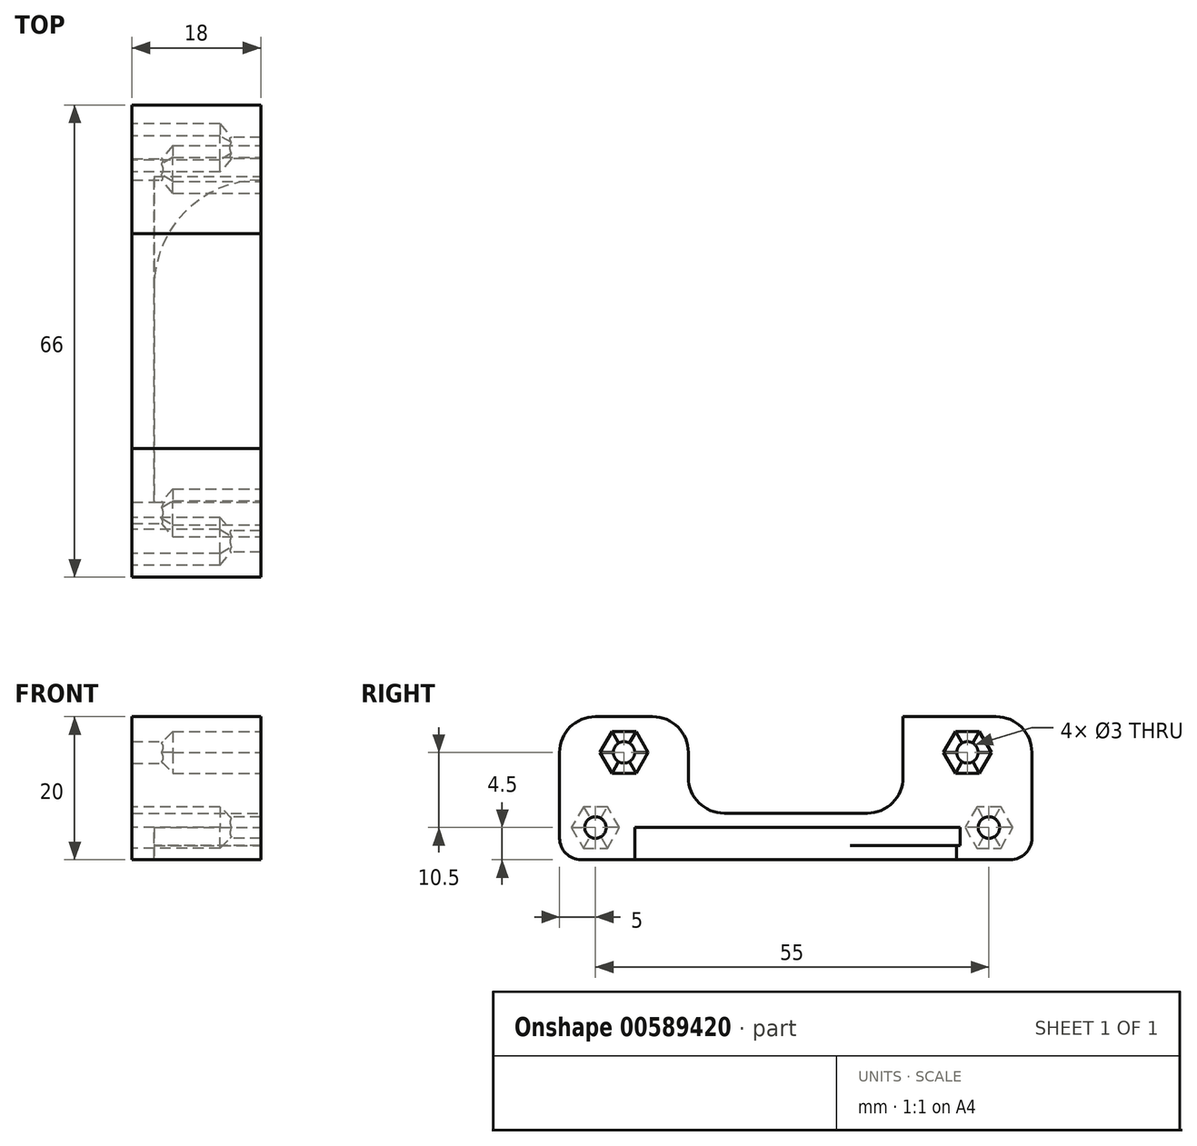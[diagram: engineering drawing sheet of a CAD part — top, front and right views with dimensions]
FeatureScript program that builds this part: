
annotation { "Feature Type Name" : "Feature", "Feature Type Description" : "" }
export const myFeature = defineFeature(function(context is Context, id is Id, definition is map)
    precondition{}
    {
        {
            var Q0;
            Q0=qCreatedBy(makeId("Right.planeOp"),FACE);
            var sketch = newSketch(context, id + "F0", { "sketchPlane" : qUnion([Q0])});
            skLineSegment(sketch, "E0", {"start": v(0, 0) * mm, "end": v(0, 20) * mm});
            skLineSegment(sketch, "E1", {"start": v(0, 20) * mm, "end": v(10, 20) * mm});
            skLineSegment(sketch, "E2", {"start": v(10, 20) * mm, "end": v(10, 18) * mm});
            skLineSegment(sketch, "E3", {"start": v(10, 18) * mm, "end": v(5, 18) * mm});
            skLineSegment(sketch, "E4", {"start": v(5, 18) * mm, "end": v(5, 9) * mm});
            skLineSegment(sketch, "E5", {"start": v(5, 9) * mm, "end": v(66, 9) * mm});
            skLineSegment(sketch, "E6", {"start": v(66, 9) * mm, "end": v(66, 0) * mm});
            skLineSegment(sketch, "E7", {"start": v(66, 0) * mm, "end": v(0, 0) * mm});
            skLineSegment(sketch, "E8", {"start": v(66, 9) * mm, "end": v(66, 20) * mm});
            skLineSegment(sketch, "E9", {"start": v(66, 20) * mm, "end": v(10, 20) * mm});
            skSolve(sketch);
        }
        {
            var Q0;
            Q0=makeQuery(id+"F0.imprint","IMPRINT",FACE,{"disambiguationData":[TD([[makeQuery(id+"F0.imprint","IMPRINT",EDGE,{"derivedFrom":sQuery(id+"F0.wireOp",EDGE,"E0")}),-1.0]])]});
            var Q1;
            Q1=makeQuery(id+"F0.imprint","IMPRINT",FACE,{"disambiguationData":[TD([[makeQuery(id+"F0.imprint","IMPRINT",EDGE,{"derivedFrom":sQuery(id+"F0.wireOp",EDGE,"E2")}),1.0]])]});
            extrude(context, id + "F1", {"entities" : qUnion([Q0, Q1]), "oppositeDirection" : true, "depth" : 16 * mm, "offsetDistance" : 25 * mm});
        }
        {
            var Q0;
            Q0=makeQuery(id+"F1.opExtrude","CAP_FACE",FACE,{"disambiguationData":[OSD([sQuery(id+"F0.wireOp",EDGE,"E0"),sQuery(id+"F0.wireOp",EDGE,"E1"),sQuery(id+"F0.wireOp",EDGE,"E2"),sQuery(id+"F0.wireOp",EDGE,"E3"),sQuery(id+"F0.wireOp",EDGE,"E4"),sQuery(id+"F0.wireOp",EDGE,"E5"),sQuery(id+"F0.wireOp",EDGE,"E6"),sQuery(id+"F0.wireOp",EDGE,"E7")])],"isStart":true});
            var sketch = newSketch(context, id + "F2", { "sketchPlane" : qUnion([Q0])});
            skLineSegment(sketch, "E10.0", {"start": v(66, 0) * mm, "end": v(0, 0) * mm});
            skLineSegment(sketch, "E11", {"start": v(10.5, 0) * mm, "end": v(10.5, 4.5) * mm});
            skLineSegment(sketch, "E12", {"start": v(10.5, 4.5) * mm, "end": v(56, 4.5) * mm});
            skLineSegment(sketch, "E13", {"start": v(56, 4.5) * mm, "end": v(56, 2) * mm});
            skLineSegment(sketch, "E14", {"start": v(56, 2) * mm, "end": v(55.5, 2) * mm});
            skLineSegment(sketch, "E15", {"start": v(55.5, 2) * mm, "end": v(55.5, 0) * mm});
            skSolve(sketch);
        }
        {
            var Q0;
            {var subQ0=sQuery(id+"F2.wireOp",EDGE,"E11");Q0=makeQuery(id+"F2.imprint","IMPRINT",FACE,{"disambiguationData":[TD([[makeQuery(id+"F2.imprint","IMPRINT",EDGE,{"derivedFrom":subQ0}),-1.0]])]});}
            extrude(context, id + "F3", {"entities" : qUnion([Q0]), "operationType" : NewBodyOperationType.REMOVE, "oppositeDirection" : true, "depth" : 14.9 * mm});
        }
        {
            var Q0;
            Q0=makeQuery(id+"F1.opExtrude","SWEPT_FACE",FACE,{"disambiguationData":[OSD([sQuery(id+"F0.wireOp",EDGE,"E7")])]});
            var sketch = newSketch(context, id + "F4", { "sketchPlane" : qUnion([Q0])});
            skLineSegment(sketch, "E16.0", {"start": v(-14.9, -55.5) * mm, "end": v(0, -55.5) * mm});
            skLineSegment(sketch, "E17.0", {"start": v(-14.9, -55.5) * mm, "end": v(-14.9, -10.5) * mm});
            skArc(sketch, "E18", {"start": v(-14.9, -40.6) * mm, "mid": v(-10.54, -51.14) * mm, "end": v(0, -55.5) * mm});
            skSolve(sketch);
        }
        {
            var Q0;
            {var subQ0=sQuery(id+"F4.wireOp",EDGE,"E16.0");Q0=makeQuery(id+"F4.imprint","IMPRINT",FACE,{"disambiguationData":[TD([[makeQuery(id+"F4.imprint","IMPRINT",EDGE,{"derivedFrom":subQ0}),1.0]])]});}
            var Q1;
            Q1=makeQuery(id+"F3.boolean.opBoolean","COPY",FACE,{"derivedFrom":makeQuery(id+"F3.opExtrude","SWEPT_FACE",FACE,{"disambiguationData":[OSD([sQuery(id+"F2.wireOp",EDGE,"E14")])]})});
            extrude(context, id + "F5", {"entities" : qUnion([Q0]), "operationType" : NewBodyOperationType.ADD, "endBound" : BoundingType.UP_TO_SURFACE, "oppositeDirection" : true, "endBoundEntityFace" : qUnion([Q1]), "depth" : 2 * mm});
        }
        {
            var Q0;
            Q0=makeQuery(id+"F1.opExtrude","CAP_FACE",FACE,{"disambiguationData":[OSD([sQuery(id+"F0.wireOp",EDGE,"E0"),sQuery(id+"F0.wireOp",EDGE,"E1"),sQuery(id+"F0.wireOp",EDGE,"E2"),sQuery(id+"F0.wireOp",EDGE,"E3"),sQuery(id+"F0.wireOp",EDGE,"E4"),sQuery(id+"F0.wireOp",EDGE,"E5"),sQuery(id+"F0.wireOp",EDGE,"E6"),sQuery(id+"F0.wireOp",EDGE,"E7")])],"isStart":false});
            var sketch = newSketch(context, id + "F6", { "sketchPlane" : qUnion([Q0])});
            skLineSegment(sketch, "E19.0", {"start": v(-66, 0) * mm, "end": v(0, 0) * mm});
            skLineSegment(sketch, "E20.0", {"start": v(0, 0) * mm, "end": v(0, 20) * mm});
            skLineSegment(sketch, "E21", {"start": v(-66, 0) * mm, "end": v(-66, 20) * mm});
            skLineSegment(sketch, "E22", {"start": v(-66, 20) * mm, "end": v(0, 20) * mm});
            skSolve(sketch);
        }
        {
            var Q0;
            {var subQ2=sQuery(id+"F6.wireOp",EDGE,"E19.0");Q0=makeQuery(id+"F6.imprint","IMPRINT",FACE,{"disambiguationData":[TD([[makeQuery(id+"F6.imprint","IMPRINT",EDGE,{"derivedFrom":subQ2}),1.0]])]});}
            var Q1;
            {var subQ0=makeQuery(id+"F1.opExtrude","CAP_EDGE",EDGE,{"disambiguationData":[OSD([sQuery(id+"F0.wireOp",EDGE,"E2")])],"isStart":false});Q1=makeQuery(id+"F6.imprint","IMPRINT",FACE,{"disambiguationData":[TD([[makeQuery(id+"F6.imprint","IMPRINT",EDGE,{"derivedFrom":subQ0}),-1.0]])]});}
            extrude(context, id + "F7", {"entities" : qUnion([Q0, Q1]), "operationType" : NewBodyOperationType.ADD, "depth" : 2 * mm, "offsetDistance" : 25 * mm});
        }
        {
            var Q0;
            Q0=makeQuery(id+"F7.boolean.opBoolean","MERGE",EDGE,{"derivedFrom":[makeQuery(id+"F1.opExtrude","SWEPT_EDGE",EDGE,{"disambiguationData":[OSD([sQuery(id+"F0.wireOp",EDGE,"E6"),sQuery(id+"F0.wireOp",EDGE,"E7")])]}),makeQuery(id+"F7.opExtrude","SWEPT_EDGE",EDGE,{"disambiguationData":[OSD([sQuery(id+"F6.wireOp",EDGE,"E19.0"),sQuery(id+"F6.wireOp",EDGE,"E21")])]})]});
            var Q1;
            Q1=makeQuery(id+"F3.boolean.opBoolean","COPY",EDGE,{"derivedFrom":makeQuery(id+"F3.opExtrude","SWEPT_EDGE",EDGE,{"disambiguationData":[OSD([sQuery(id+"F2.wireOp",EDGE,"E10.0"),sQuery(id+"F2.wireOp",EDGE,"E11")])]})});
            var Q2;
            Q2=makeQuery(id+"F7.boolean.opBoolean","MERGE",EDGE,{"derivedFrom":[makeQuery(id+"F1.opExtrude","SWEPT_EDGE",EDGE,{"disambiguationData":[OSD([sQuery(id+"F0.wireOp",EDGE,"E0"),sQuery(id+"F0.wireOp",EDGE,"E7")])]}),makeQuery(id+"F7.opExtrude","SWEPT_EDGE",EDGE,{"disambiguationData":[OSD([sQuery(id+"F6.wireOp",EDGE,"E19.0"),sQuery(id+"F6.wireOp",EDGE,"E20.0")])]})]});
            fillet(context, id + "F8", {"entities" : qUnion([Q0, Q1, Q2]), "radius" : 3 * mm, "tangentPropagation" : true, "allowEdgeOverflow" : false});
        }
        {
            var Q0;
            Q0=makeQuery(id+"F7.opExtrude","CAP_FACE",FACE,{"disambiguationData":[OSD([sQuery(id+"F6.wireOp",EDGE,"E19.0"),sQuery(id+"F6.wireOp",EDGE,"E20.0"),sQuery(id+"F6.wireOp",EDGE,"E21"),sQuery(id+"F6.wireOp",EDGE,"E22")])],"isStart":false});
            var sketch = newSketch(context, id + "F9", { "sketchPlane" : qUnion([Q0])});
            skCircle(sketch, "E23.cCircle", {"center": v(-60, 4.5) * mm, "radius": 2.9 * mm, "construction": true});
            skLineSegment(sketch, "E23.0", {"start": v(-63.35, 4.5) * mm, "end": v(-61.67, 7.4) * mm});
            skLineSegment(sketch, "E23.1", {"start": v(-61.67, 7.4) * mm, "end": v(-58.33, 7.4) * mm});
            skLineSegment(sketch, "E23.2", {"start": v(-58.33, 7.4) * mm, "end": v(-56.65, 4.5) * mm});
            skLineSegment(sketch, "E23.3", {"start": v(-56.65, 4.5) * mm, "end": v(-58.33, 1.6) * mm});
            skLineSegment(sketch, "E23.4", {"start": v(-58.33, 1.6) * mm, "end": v(-61.67, 1.6) * mm});
            skLineSegment(sketch, "E23.5", {"start": v(-61.67, 1.6) * mm, "end": v(-63.35, 4.5) * mm});
            skPoint(sketch, "E23.0.midPoint", {"position": v(-62.51, 5.95) * mm});
            skLineSegment(sketch, "E24.1.0.0", {"start": v(-6.67, 1.6) * mm, "end": v(-8.35, 4.5) * mm});
            skPoint(sketch, "E24.1.0.1", {"position": v(-7.51, 5.95) * mm});
            skCircle(sketch, "E24.1.0.2", {"center": v(-5, 4.5) * mm, "radius": 2.9 * mm, "construction": true});
            skLineSegment(sketch, "E24.1.0.3", {"start": v(-8.35, 4.5) * mm, "end": v(-6.67, 7.4) * mm});
            skLineSegment(sketch, "E24.1.0.4", {"start": v(-6.67, 7.4) * mm, "end": v(-3.33, 7.4) * mm});
            skLineSegment(sketch, "E24.1.0.5", {"start": v(-3.33, 7.4) * mm, "end": v(-1.65, 4.5) * mm});
            skLineSegment(sketch, "E24.1.0.6", {"start": v(-1.65, 4.5) * mm, "end": v(-3.33, 1.6) * mm});
            skLineSegment(sketch, "E24.1.0.7", {"start": v(-3.33, 1.6) * mm, "end": v(-6.67, 1.6) * mm});
            skLineSegment(sketch, "E24.2.0.0", {"start": v(48.33, 1.6) * mm, "end": v(46.65, 4.5) * mm});
            skPoint(sketch, "E24.2.0.1", {"position": v(47.49, 5.95) * mm});
            skCircle(sketch, "E24.2.0.2", {"center": v(50, 4.5) * mm, "radius": 2.9 * mm, "construction": true});
            skLineSegment(sketch, "E24.2.0.3", {"start": v(46.65, 4.5) * mm, "end": v(48.33, 7.4) * mm});
            skLineSegment(sketch, "E24.2.0.4", {"start": v(48.33, 7.4) * mm, "end": v(51.67, 7.4) * mm});
            skLineSegment(sketch, "E24.2.0.5", {"start": v(51.67, 7.4) * mm, "end": v(53.35, 4.5) * mm});
            skLineSegment(sketch, "E24.2.0.6", {"start": v(53.35, 4.5) * mm, "end": v(51.67, 1.6) * mm});
            skLineSegment(sketch, "E24.2.0.7", {"start": v(51.67, 1.6) * mm, "end": v(48.33, 1.6) * mm});
            skLineSegment(sketch, "E24.direction1", {"start": v(-61.67, 1.6) * mm, "end": v(-6.67, 1.6) * mm, "construction": true});
            skSolve(sketch);
        }
        {
            var Q0;
            Q0=makeQuery(id+"F9.imprint","IMPRINT",FACE,{"disambiguationData":[TD([[makeQuery(id+"F9.imprint","IMPRINT",EDGE,{"derivedFrom":sQuery(id+"F9.wireOp",EDGE,"E23.0")}),-1.0]])]});
            var Q1;
            Q1=makeQuery(id+"F9.imprint","IMPRINT",FACE,{"disambiguationData":[TD([[makeQuery(id+"F9.imprint","IMPRINT",EDGE,{"derivedFrom":sQuery(id+"F9.wireOp",EDGE,"E24.1.0.0")}),-1.0]])]});
            extrude(context, id + "F10", {"entities" : qUnion([Q0, Q1]), "operationType" : NewBodyOperationType.REMOVE, "oppositeDirection" : true, "depth" : 14 * mm, "offsetDistance" : 25 * mm});
        }
        {
            var Q0;
            Q0=makeQuery(id+"F10.boolean.opBoolean","COPY",EDGE,{"derivedFrom":makeQuery(id+"F10.opExtrude","CAP_EDGE",EDGE,{"disambiguationData":[OSD([sQuery(id+"F9.wireOp",EDGE,"E23.0")])],"isStart":false})});
            var Q1;
            Q1=makeQuery(id+"F10.boolean.opBoolean","COPY",EDGE,{"derivedFrom":makeQuery(id+"F10.opExtrude","CAP_EDGE",EDGE,{"disambiguationData":[OSD([sQuery(id+"F9.wireOp",EDGE,"E23.1")])],"isStart":false})});
            var Q2;
            Q2=makeQuery(id+"F10.boolean.opBoolean","COPY",EDGE,{"derivedFrom":makeQuery(id+"F10.opExtrude","CAP_EDGE",EDGE,{"disambiguationData":[OSD([sQuery(id+"F9.wireOp",EDGE,"E23.5")])],"isStart":false})});
            var Q3;
            Q3=makeQuery(id+"F10.boolean.opBoolean","COPY",FACE,{"derivedFrom":makeQuery(id+"F10.opExtrude","CAP_FACE",FACE,{"disambiguationData":[OSD([sQuery(id+"F9.wireOp",EDGE,"E23.0"),sQuery(id+"F9.wireOp",EDGE,"E23.1"),sQuery(id+"F9.wireOp",EDGE,"E23.2"),sQuery(id+"F9.wireOp",EDGE,"E23.3"),sQuery(id+"F9.wireOp",EDGE,"E23.4"),sQuery(id+"F9.wireOp",EDGE,"E23.5")])],"isStart":false})});
            var Q4;
            Q4=makeQuery(id+"F10.boolean.opBoolean","COPY",FACE,{"derivedFrom":makeQuery(id+"F10.opExtrude","CAP_FACE",FACE,{"disambiguationData":[OSD([sQuery(id+"F9.wireOp",EDGE,"E24.1.0.0"),sQuery(id+"F9.wireOp",EDGE,"E24.1.0.3"),sQuery(id+"F9.wireOp",EDGE,"E24.1.0.4"),sQuery(id+"F9.wireOp",EDGE,"E24.1.0.5"),sQuery(id+"F9.wireOp",EDGE,"E24.1.0.6"),sQuery(id+"F9.wireOp",EDGE,"E24.1.0.7")])],"isStart":false})});
            chamfer(context, id + "F11", {"entities" : qUnion([Q0, Q1, Q2, Q3, Q4]), "width" : 1.7 * mm, "tangentPropagation" : true});
        }
        {
            var Q0;
            Q0=makeQuery(id+"F7.opExtrude","CAP_FACE",FACE,{"disambiguationData":[OSD([sQuery(id+"F6.wireOp",EDGE,"E19.0"),sQuery(id+"F6.wireOp",EDGE,"E20.0"),sQuery(id+"F6.wireOp",EDGE,"E21"),sQuery(id+"F6.wireOp",EDGE,"E22")])],"isStart":false});
            var sketch = newSketch(context, id + "F12", { "sketchPlane" : qUnion([Q0])});
            skPoint(sketch, "E25.0", {"position": v(-60, 1.6) * mm});
            skPoint(sketch, "E26.0", {"position": v(-60, 7.4) * mm});
            skLineSegment(sketch, "E27", {"start": v(-60, 7.4) * mm, "end": v(-60, 1.6) * mm, "construction": true});
            skPoint(sketch, "E28", {"position": v(-60, 4.5) * mm});
            skPoint(sketch, "E29.0", {"position": v(-5, 7.4) * mm});
            skPoint(sketch, "E30.0", {"position": v(-5, 1.6) * mm});
            skLineSegment(sketch, "E31", {"start": v(-5, 7.4) * mm, "end": v(-5, 1.6) * mm, "construction": true});
            skPoint(sketch, "E32", {"position": v(-5, 4.5) * mm});
            skSolve(sketch);
        }
        {
            var Q0;
            Q0=sQuery(id+"F12.wireOp",VERTEX,"E28");
            var Q1;
            Q1=sQuery(id+"F12.wireOp",VERTEX,"E32");
            var Q2;
            Q2=makeQuery(id+"F1.opExtrude","SWEPT_BODY",BODY,{"disambiguationData":[OSD([sQuery(id+"F0.wireOp",EDGE,"E0"),sQuery(id+"F0.wireOp",EDGE,"E1"),sQuery(id+"F0.wireOp",EDGE,"E2"),sQuery(id+"F0.wireOp",EDGE,"E3"),sQuery(id+"F0.wireOp",EDGE,"E4"),sQuery(id+"F0.wireOp",EDGE,"E5"),sQuery(id+"F0.wireOp",EDGE,"E6"),sQuery(id+"F0.wireOp",EDGE,"E7")])]});
            hole(context, id + "F13", {"style" : HoleStyle.SIMPLE, "endStyle" : HoleEndStyle.THROUGH, "holeDiameter" : 3 * mm, "isTappedThrough" : true, "tappedDepth" : 12 * mm, "tapClearance" : 3, "locations" : qUnion([Q0, Q1]), "scope" : qUnion([Q2])});
        }
        {
            var Q0;
            Q0=makeQuery(id+"F7.boolean.opBoolean","MERGE",EDGE,{"derivedFrom":[makeQuery(id+"F1.opExtrude","SWEPT_EDGE",EDGE,{"disambiguationData":[OSD([sQuery(id+"F0.wireOp",EDGE,"E8"),sQuery(id+"F0.wireOp",EDGE,"E9")])]}),makeQuery(id+"F7.opExtrude","SWEPT_EDGE",EDGE,{"disambiguationData":[OSD([sQuery(id+"F6.wireOp",EDGE,"E21"),sQuery(id+"F6.wireOp",EDGE,"E22")])]})]});
            var Q1;
            Q1=makeQuery(id+"F7.boolean.opBoolean","MERGE",EDGE,{"derivedFrom":[makeQuery(id+"F1.opExtrude","SWEPT_EDGE",EDGE,{"disambiguationData":[OSD([sQuery(id+"F0.wireOp",EDGE,"E0"),sQuery(id+"F0.wireOp",EDGE,"E1")])]}),makeQuery(id+"F7.opExtrude","SWEPT_EDGE",EDGE,{"disambiguationData":[OSD([sQuery(id+"F6.wireOp",EDGE,"E20.0"),sQuery(id+"F6.wireOp",EDGE,"E22")])]})]});
            fillet(context, id + "F14", {"entities" : qUnion([Q0, Q1]), "radius" : 5 * mm, "tangentPropagation" : true, "allowEdgeOverflow" : false});
        }
        {
            var Q0;
            Q0=makeQuery(id+"F1.opExtrude","CAP_FACE",FACE,{"disambiguationData":[OSD([sQuery(id+"F0.wireOp",EDGE,"E0"),sQuery(id+"F0.wireOp",EDGE,"E1"),sQuery(id+"F0.wireOp",EDGE,"E6"),sQuery(id+"F0.wireOp",EDGE,"E7"),sQuery(id+"F0.wireOp",EDGE,"E8"),sQuery(id+"F0.wireOp",EDGE,"E9")])],"isStart":true});
            var sketch = newSketch(context, id + "F15", { "sketchPlane" : qUnion([Q0])});
            skLineSegment(sketch, "E33", {"start": v(57, 15) * mm, "end": v(9, 15) * mm});
            skPoint(sketch, "E34.0", {"position": v(33, 20) * mm});
            skLineSegment(sketch, "E35", {"start": v(33, 20) * mm, "end": v(33, 15) * mm, "construction": true});
            skSolve(sketch);
        }
        {
            var Q0;
            Q0=sQuery(id+"F15.wireOp",VERTEX,"E33.start");
            var Q1;
            Q1=sQuery(id+"F15.wireOp",VERTEX,"E33.end");
            var Q2;
            Q2=makeQuery(id+"F1.opExtrude","SWEPT_BODY",BODY,{"disambiguationData":[OSD([sQuery(id+"F0.wireOp",EDGE,"E0"),sQuery(id+"F0.wireOp",EDGE,"E1"),sQuery(id+"F0.wireOp",EDGE,"E6"),sQuery(id+"F0.wireOp",EDGE,"E7"),sQuery(id+"F0.wireOp",EDGE,"E8"),sQuery(id+"F0.wireOp",EDGE,"E9")])]});
            hole(context, id + "F16", {"style" : HoleStyle.SIMPLE, "endStyle" : HoleEndStyle.THROUGH, "holeDiameter" : 3 * mm, "isTappedThrough" : true, "tappedDepth" : 12 * mm, "tapClearance" : 3, "locations" : qUnion([Q0, Q1]), "scope" : qUnion([Q2])});
        }
        {
            var Q0;
            Q0=makeQuery(id+"F1.opExtrude","CAP_FACE",FACE,{"disambiguationData":[OSD([sQuery(id+"F0.wireOp",EDGE,"E0"),sQuery(id+"F0.wireOp",EDGE,"E1"),sQuery(id+"F0.wireOp",EDGE,"E6"),sQuery(id+"F0.wireOp",EDGE,"E7"),sQuery(id+"F0.wireOp",EDGE,"E8"),sQuery(id+"F0.wireOp",EDGE,"E9")])],"isStart":true});
            var sketch = newSketch(context, id + "F17", { "sketchPlane" : qUnion([Q0])});
            skCircle(sketch, "E36.0", {"center": v(57, 15) * mm, "radius": 1.5 * mm});
            skCircle(sketch, "E37.0", {"center": v(9, 15) * mm, "radius": 1.5 * mm});
            skCircle(sketch, "E38.cCircle", {"center": v(57, 15) * mm, "radius": 2.9 * mm, "construction": true});
            skLineSegment(sketch, "E38.0", {"start": v(60.35, 15) * mm, "end": v(58.67, 12.1) * mm});
            skLineSegment(sketch, "E38.1", {"start": v(58.67, 12.1) * mm, "end": v(55.33, 12.1) * mm});
            skLineSegment(sketch, "E38.2", {"start": v(55.33, 12.1) * mm, "end": v(53.65, 15) * mm});
            skLineSegment(sketch, "E38.3", {"start": v(53.65, 15) * mm, "end": v(55.33, 17.9) * mm});
            skLineSegment(sketch, "E38.4", {"start": v(55.33, 17.9) * mm, "end": v(58.67, 17.9) * mm});
            skLineSegment(sketch, "E38.5", {"start": v(58.67, 17.9) * mm, "end": v(60.35, 15) * mm});
            skPoint(sketch, "E38.0.midPoint", {"position": v(59.51, 13.55) * mm});
            skCircle(sketch, "E39.cCircle", {"center": v(9, 15) * mm, "radius": 2.9 * mm, "construction": true});
            skLineSegment(sketch, "E39.0", {"start": v(12.35, 15) * mm, "end": v(10.67, 12.1) * mm});
            skLineSegment(sketch, "E39.1", {"start": v(10.67, 12.1) * mm, "end": v(7.33, 12.1) * mm});
            skLineSegment(sketch, "E39.2", {"start": v(7.33, 12.1) * mm, "end": v(5.65, 15) * mm});
            skLineSegment(sketch, "E39.3", {"start": v(5.65, 15) * mm, "end": v(7.33, 17.9) * mm});
            skLineSegment(sketch, "E39.4", {"start": v(7.33, 17.9) * mm, "end": v(10.67, 17.9) * mm});
            skLineSegment(sketch, "E39.5", {"start": v(10.67, 17.9) * mm, "end": v(12.35, 15) * mm});
            skPoint(sketch, "E39.0.midPoint", {"position": v(11.51, 13.55) * mm});
            skSolve(sketch);
        }
        {
            var Q0;
            Q0=makeQuery(id+"F17.imprint","IMPRINT",FACE,{"disambiguationData":[TD([[makeQuery(id+"F17.imprint","IMPRINT",EDGE,{"derivedFrom":sQuery(id+"F17.wireOp",EDGE,"E37.0")}),-1.0]])]});
            var Q1;
            Q1=makeQuery(id+"F17.imprint","IMPRINT",FACE,{"disambiguationData":[TD([[makeQuery(id+"F17.imprint","IMPRINT",EDGE,{"derivedFrom":sQuery(id+"F17.wireOp",EDGE,"E36.0")}),-1.0]])]});
            extrude(context, id + "F18", {"entities" : qUnion([Q0, Q1]), "operationType" : NewBodyOperationType.REMOVE, "oppositeDirection" : true, "depth" : 14 * mm, "offsetDistance" : 25 * mm});
        }
        {
            var Q0;
            Q0=makeQuery(id+"F18.boolean.opBoolean","COPY",EDGE,{"derivedFrom":makeQuery(id+"F18.opExtrude","CAP_EDGE",EDGE,{"disambiguationData":[OSD([sQuery(id+"F17.wireOp",EDGE,"E38.0")])],"isStart":false})});
            var Q1;
            Q1=makeQuery(id+"F18.boolean.opBoolean","COPY",EDGE,{"derivedFrom":makeQuery(id+"F18.opExtrude","CAP_EDGE",EDGE,{"disambiguationData":[OSD([sQuery(id+"F17.wireOp",EDGE,"E38.5")])],"isStart":false})});
            var Q2;
            Q2=makeQuery(id+"F18.boolean.opBoolean","COPY",EDGE,{"derivedFrom":makeQuery(id+"F18.opExtrude","CAP_EDGE",EDGE,{"disambiguationData":[OSD([sQuery(id+"F17.wireOp",EDGE,"E38.4")])],"isStart":false})});
            var Q3;
            Q3=makeQuery(id+"F18.boolean.opBoolean","COPY",EDGE,{"derivedFrom":makeQuery(id+"F18.opExtrude","CAP_EDGE",EDGE,{"disambiguationData":[OSD([sQuery(id+"F17.wireOp",EDGE,"E38.3")])],"isStart":false})});
            var Q4;
            Q4=makeQuery(id+"F18.boolean.opBoolean","COPY",EDGE,{"derivedFrom":makeQuery(id+"F18.opExtrude","CAP_EDGE",EDGE,{"disambiguationData":[OSD([sQuery(id+"F17.wireOp",EDGE,"E38.2")])],"isStart":false})});
            var Q5;
            Q5=makeQuery(id+"F18.boolean.opBoolean","COPY",EDGE,{"derivedFrom":makeQuery(id+"F18.opExtrude","CAP_EDGE",EDGE,{"disambiguationData":[OSD([sQuery(id+"F17.wireOp",EDGE,"E38.1")])],"isStart":false})});
            var Q6;
            Q6=makeQuery(id+"F18.boolean.opBoolean","COPY",EDGE,{"derivedFrom":makeQuery(id+"F18.opExtrude","CAP_EDGE",EDGE,{"disambiguationData":[OSD([sQuery(id+"F17.wireOp",EDGE,"E39.1")])],"isStart":false})});
            var Q7;
            Q7=makeQuery(id+"F18.boolean.opBoolean","COPY",EDGE,{"derivedFrom":makeQuery(id+"F18.opExtrude","CAP_EDGE",EDGE,{"disambiguationData":[OSD([sQuery(id+"F17.wireOp",EDGE,"E39.0")])],"isStart":false})});
            var Q8;
            Q8=makeQuery(id+"F18.boolean.opBoolean","COPY",EDGE,{"derivedFrom":makeQuery(id+"F18.opExtrude","CAP_EDGE",EDGE,{"disambiguationData":[OSD([sQuery(id+"F17.wireOp",EDGE,"E39.5")])],"isStart":false})});
            var Q9;
            Q9=makeQuery(id+"F18.boolean.opBoolean","COPY",EDGE,{"derivedFrom":makeQuery(id+"F18.opExtrude","CAP_EDGE",EDGE,{"disambiguationData":[OSD([sQuery(id+"F17.wireOp",EDGE,"E39.4")])],"isStart":false})});
            var Q10;
            Q10=makeQuery(id+"F18.boolean.opBoolean","COPY",EDGE,{"derivedFrom":makeQuery(id+"F18.opExtrude","CAP_EDGE",EDGE,{"disambiguationData":[OSD([sQuery(id+"F17.wireOp",EDGE,"E39.3")])],"isStart":false})});
            var Q11;
            Q11=makeQuery(id+"F18.boolean.opBoolean","COPY",EDGE,{"derivedFrom":makeQuery(id+"F18.opExtrude","CAP_EDGE",EDGE,{"disambiguationData":[OSD([sQuery(id+"F17.wireOp",EDGE,"E39.2")])],"isStart":false})});
            chamfer(context, id + "F19", {"entities" : qUnion([Q0, Q1, Q2, Q3, Q4, Q5, Q6, Q7, Q8, Q9, Q10, Q11]), "width" : 1.7 * mm, "tangentPropagation" : true});
        }
        {
            var Q0;
            Q0=makeQuery(id+"F1.opExtrude","CAP_FACE",FACE,{"disambiguationData":[OSD([sQuery(id+"F0.wireOp",EDGE,"E0"),sQuery(id+"F0.wireOp",EDGE,"E1"),sQuery(id+"F0.wireOp",EDGE,"E6"),sQuery(id+"F0.wireOp",EDGE,"E7"),sQuery(id+"F0.wireOp",EDGE,"E8"),sQuery(id+"F0.wireOp",EDGE,"E9")])],"isStart":true});
            var sketch = newSketch(context, id + "F20", { "sketchPlane" : qUnion([Q0])});
            skLineSegment(sketch, "E40.bottom", {"start": v(48, 20) * mm, "end": v(18, 20) * mm});
            skLineSegment(sketch, "E40.top", {"start": v(48, 6.5) * mm, "end": v(18, 6.5) * mm});
            skLineSegment(sketch, "E40.left", {"start": v(48, 20) * mm, "end": v(48, 6.5) * mm});
            skLineSegment(sketch, "E40.right", {"start": v(18, 20) * mm, "end": v(18, 6.5) * mm});
            skPoint(sketch, "E41.0", {"position": v(33, 20) * mm});
            skSolve(sketch);
        }
        {
            var Q0;
            Q0=makeQuery(id+"F20.imprint","IMPRINT",FACE,{"disambiguationData":[TD([[makeQuery(id+"F20.imprint","IMPRINT",EDGE,{"derivedFrom":sQuery(id+"F20.wireOp",EDGE,"E40.bottom")}),-1.0]])]});
            extrude(context, id + "F21", {"entities" : qUnion([Q0]), "operationType" : NewBodyOperationType.REMOVE, "endBound" : BoundingType.THROUGH_ALL, "oppositeDirection" : true, "depth" : 25 * mm, "offsetDistance" : 25 * mm});
        }
        {
            var Q0;
            Q0=makeQuery(id+"F21.boolean.opBoolean","COPY",EDGE,{"derivedFrom":makeQuery(id+"F21.opExtrude","SWEPT_EDGE",EDGE,{"disambiguationData":[OSD([sQuery(id+"F0.wireOp",EDGE,"E1"),sQuery(id+"F0.wireOp",EDGE,"E9"),sQuery(id+"F20.wireOp",EDGE,"E40.bottom"),sQuery(id+"F20.wireOp",EDGE,"E40.left")])]})});
            var Q1;
            Q1=makeQuery(id+"F21.boolean.opBoolean","COPY",EDGE,{"derivedFrom":makeQuery(id+"F21.opExtrude","SWEPT_EDGE",EDGE,{"disambiguationData":[OSD([sQuery(id+"F0.wireOp",EDGE,"E1"),sQuery(id+"F0.wireOp",EDGE,"E9"),sQuery(id+"F20.wireOp",EDGE,"E40.bottom"),sQuery(id+"F20.wireOp",EDGE,"E40.right")])]})});
            fillet(context, id + "F22", {"entities" : qUnion([Q0, Q1]), "radius" : 5 * mm, "tangentPropagation" : true, "allowEdgeOverflow" : false});
        }
        {
            var Q0;
            Q0=makeQuery(id+"F21.boolean.opBoolean","COPY",EDGE,{"derivedFrom":makeQuery(id+"F21.opExtrude","SWEPT_EDGE",EDGE,{"disambiguationData":[OSD([sQuery(id+"F20.wireOp",EDGE,"E40.top"),sQuery(id+"F20.wireOp",EDGE,"E40.left")])]})});
            var Q1;
            Q1=makeQuery(id+"F21.boolean.opBoolean","COPY",EDGE,{"derivedFrom":makeQuery(id+"F21.opExtrude","SWEPT_EDGE",EDGE,{"disambiguationData":[OSD([sQuery(id+"F20.wireOp",EDGE,"E40.top"),sQuery(id+"F20.wireOp",EDGE,"E40.right")])]})});
            fillet(context, id + "F23", {"entities" : qUnion([Q0, Q1]), "radius" : 5 * mm, "tangentPropagation" : true, "allowEdgeOverflow" : false});
        }
    });
